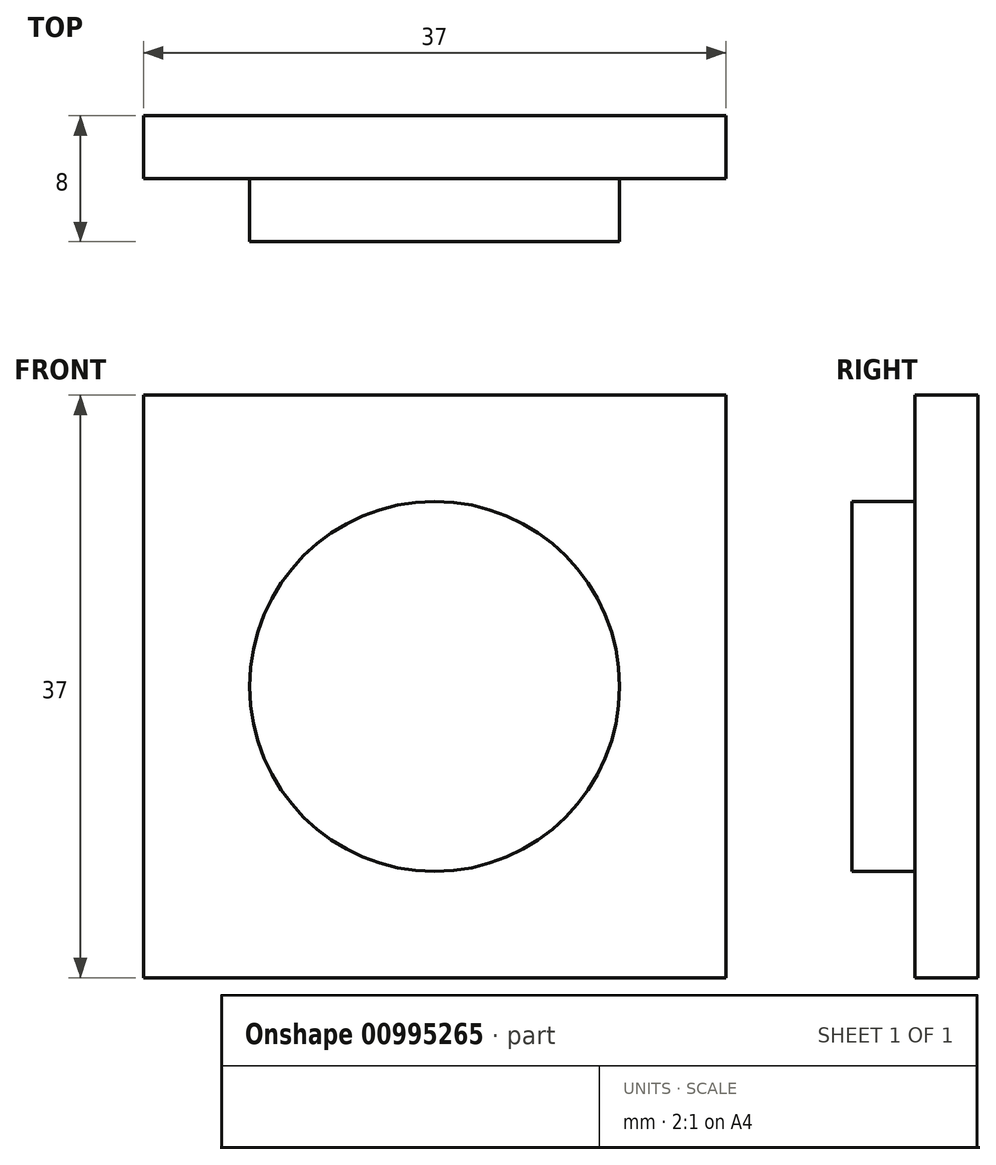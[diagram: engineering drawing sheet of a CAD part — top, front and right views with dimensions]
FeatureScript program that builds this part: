
annotation { "Feature Type Name" : "Feature", "Feature Type Description" : "" }
export const myFeature = defineFeature(function(context is Context, id is Id, definition is map)
    precondition{}
    {
        {
            var Q0;
            Q0=qCreatedBy(makeId("Front.planeOp"),FACE);
            var sketch = newSketch(context, id + "F0", { "sketchPlane" : qUnion([Q0])});
            skLineSegment(sketch, "E0.bottom", {"start": v(-18.5, 18.5) * mm, "end": v(18.5, 18.5) * mm});
            skLineSegment(sketch, "E0.top", {"start": v(-18.5, -18.5) * mm, "end": v(18.5, -18.5) * mm});
            skLineSegment(sketch, "E0.left", {"start": v(-18.5, 18.5) * mm, "end": v(-18.5, -18.5) * mm});
            skLineSegment(sketch, "E0.right", {"start": v(18.5, 18.5) * mm, "end": v(18.5, -18.5) * mm});
            skPoint(sketch, "E0.middle", {"position": v(0, 0) * mm});
            skSolve(sketch);
        }
        {
            var Q0;
            Q0=makeQuery(id+"F0.imprint","IMPRINT",FACE,{"disambiguationData":[TD([[makeQuery(id+"F0.imprint","IMPRINT",EDGE,{"derivedFrom":sQuery(id+"F0.wireOp",EDGE,"E0.bottom")}),-1.0]])]});
            extrude(context, id + "F1", {"entities" : qUnion([Q0]), "depth" : 4 * mm, "offsetDistance" : 25 * mm});
        }
        {
            var Q0;
            Q0=qCreatedBy(makeId("Front.planeOp"),FACE);
            var sketch = newSketch(context, id + "F2", { "sketchPlane" : qUnion([Q0])});
            skCircle(sketch, "E1", {"center": v(0, 0) * mm, "radius": 11.75 * mm});
            skSolve(sketch);
        }
        {
            var Q0;
            Q0 = qSketchRegion(id + "F2", true);
            extrude(context, id + "F3", {"entities" : qUnion([Q0]), "operationType" : NewBodyOperationType.ADD, "depth" : 8 * mm, "offsetDistance" : 25 * mm});
        }
    });
